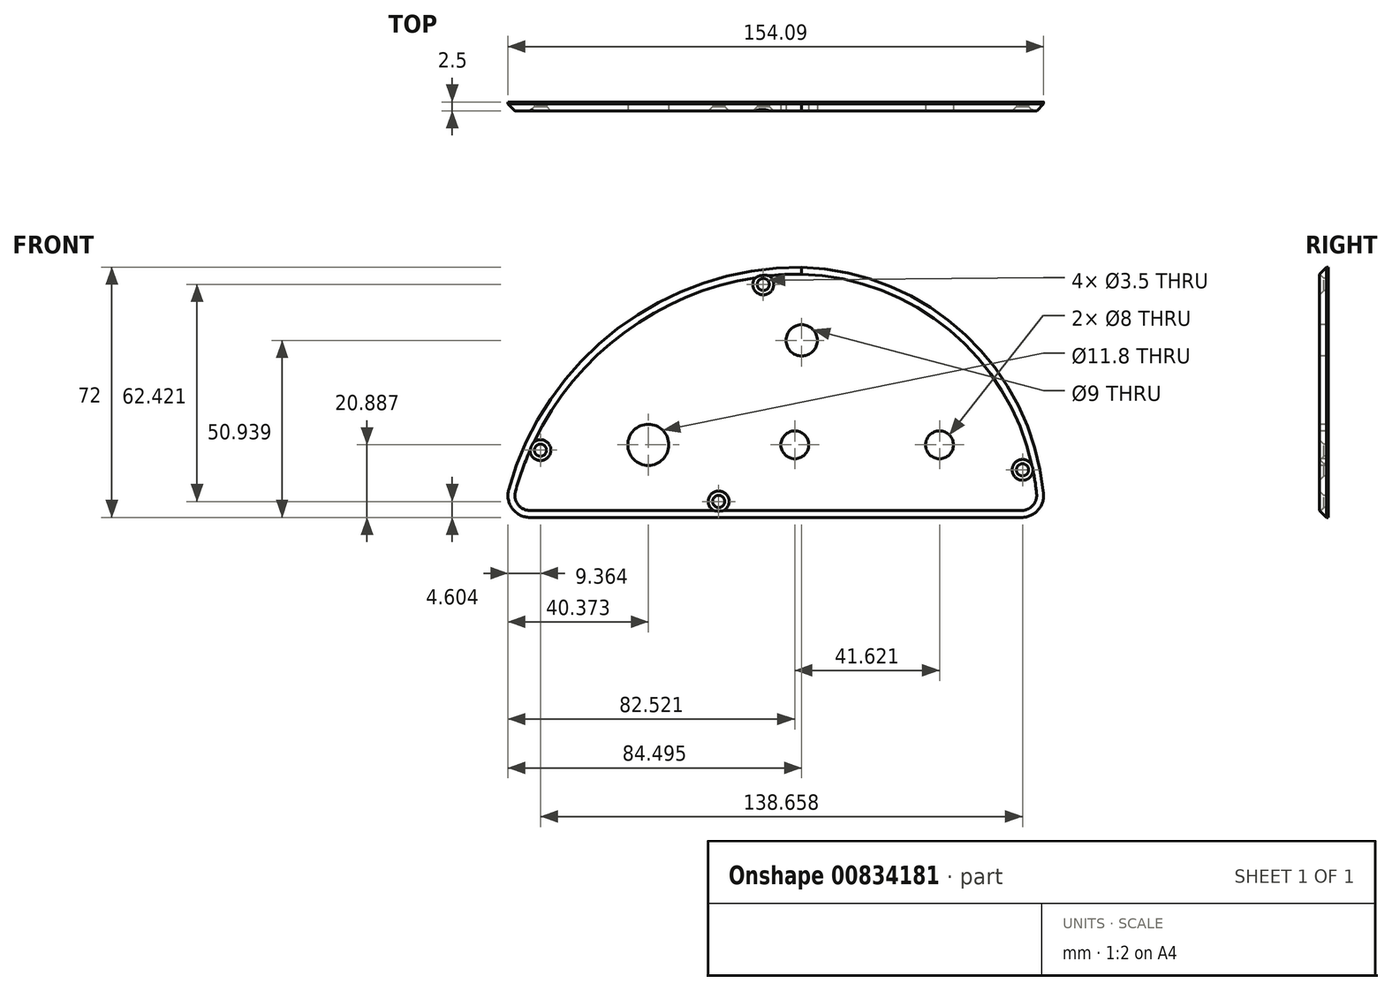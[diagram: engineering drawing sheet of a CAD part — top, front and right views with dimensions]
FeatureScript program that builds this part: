
annotation { "Feature Type Name" : "Feature", "Feature Type Description" : "" }
export const myFeature = defineFeature(function(context is Context, id is Id, definition is map)
    precondition{}
    {
        {
            var Q0;
            Q0=qCreatedBy(makeId("Front.planeOp"),FACE);
            var sketch = newSketch(context, id + "F0", { "sketchPlane" : qUnion([Q0])});
            skLineSegment(sketch, "E0", {"start": v(-103.73, 0) * mm, "end": v(52.27, 0) * mm, "construction": true});
            skLineSegment(sketch, "E1", {"start": v(-103.64, 41.04) * mm, "end": v(-17.64, 41.04) * mm, "construction": true});
            skLineSegment(sketch, "E2", {"start": v(-17.64, 0) * mm, "end": v(-17.64, 72) * mm, "construction": true});
            skArc(sketch, "E3", {"start": v(-17.64, 72) * mm, "mid": v(-70.6, 54.28) * mm, "end": v(-101.91, 8.04) * mm});
            skArc(sketch, "E4", {"start": v(51.92, 6.98) * mm, "mid": v(29.37, 52.58) * mm, "end": v(-17.64, 72) * mm});
            skLineSegment(sketch, "E5", {"start": v(-95.8, 0) * mm, "end": v(45.6, 0) * mm});
            skPoint(sketch, "E6.visualSharp", {"position": v(-103.73, 0) * mm});
            skArc(sketch, "E6.filletArc", {"start": v(-101.91, 8.04) * mm, "mid": v(-100.84, 2.5) * mm, "end": v(-95.8, 0) * mm});
            skPoint(sketch, "E7.visualSharp", {"position": v(52.27, 0) * mm});
            skArc(sketch, "E7.filletArc", {"start": v(45.6, 0) * mm, "mid": v(50.3, 2.09) * mm, "end": v(51.92, 6.98) * mm});
            skPoint(sketch, "E8", {"position": v(-28.7, 67.03) * mm});
            skPoint(sketch, "E9", {"position": v(-92.78, 19.37) * mm});
            skPoint(sketch, "E10", {"position": v(45.88, 13.7) * mm});
            skLineSegment(sketch, "E11", {"start": v(-73.3, 20.89) * mm, "end": v(34.06, 20.89) * mm, "construction": true});
            skPoint(sketch, "E12", {"position": v(-73.3, 20.89) * mm});
            skPoint(sketch, "E13", {"position": v(-19.62, 20.89) * mm});
            skPoint(sketch, "E14", {"position": v(22, 20.89) * mm});
            skPoint(sketch, "E15", {"position": v(-17.64, 50.94) * mm});
            skPoint(sketch, "E16", {"position": v(-61.77, 20.89) * mm});
            skPoint(sketch, "E17", {"position": v(-41.52, 0) * mm});
            skPoint(sketch, "E18", {"position": v(-41.52, 4.6) * mm});
            skSolve(sketch);
        }
        {
            var Q0;
            Q0=makeQuery(id+"F0.imprint","IMPRINT",FACE,{"disambiguationData":[TD([[makeQuery(id+"F0.imprint","IMPRINT",EDGE,{"derivedFrom":sQuery(id+"F0.wireOp",EDGE,"E3")}),1.0]])]});
            extrude(context, id + "F1", {"entities" : qUnion([Q0]), "oppositeDirection" : true, "depth" : 2.5 * mm, "offsetDistance" : 25 * mm});
        }
        {
            var Q0;
            Q0=sQuery(id+"F0.wireOp",VERTEX,"E9");
            var Q1;
            Q1=sQuery(id+"F0.wireOp",VERTEX,"E8");
            var Q2;
            Q2=sQuery(id+"F0.wireOp",VERTEX,"E10");
            var Q3;
            Q3=sQuery(id+"F0.wireOp",VERTEX,"E18");
            var Q4;
            Q4=makeQuery(id+"F1.opExtrude","SWEPT_BODY",BODY,{"disambiguationData":[OSD([sQuery(id+"F0.wireOp",EDGE,"E3"),sQuery(id+"F0.wireOp",EDGE,"E4"),sQuery(id+"F0.wireOp",EDGE,"E5"),sQuery(id+"F0.wireOp",EDGE,"E6.filletArc"),sQuery(id+"F0.wireOp",EDGE,"E7.filletArc")])]});
            hole(context, id + "F2", {"style" : HoleStyle.C_SINK, "endStyle" : HoleEndStyle.THROUGH, "holeDiameter" : 3.5 * mm, "cSinkDiameter" : 6 * mm, "cSinkAngle" : 90 * degree, "majorDiameter" : 5 * mm, "isTappedThrough" : true, "tappedDepth" : 12 * mm, "tapClearance" : 3, "locations" : qUnion([Q0, Q1, Q2, Q3]), "scope" : qUnion([Q4])});
        }
        {
            var Q0;
            Q0=makeQuery(id+"F1.opExtrude","CAP_EDGE",EDGE,{"disambiguationData":[OSD([sQuery(id+"F0.wireOp",EDGE,"E4")])],"isStart":true});
            chamfer(context, id + "F3", {"entities" : qUnion([Q0]), "width" : 2 * mm, "tangentPropagation" : true});
        }
        {
            var Q0;
            Q0=sQuery(id+"F0.wireOp",VERTEX,"E16");
            var Q1;
            Q1=makeQuery(id+"F1.opExtrude","SWEPT_BODY",BODY,{"disambiguationData":[OSD([sQuery(id+"F0.wireOp",EDGE,"E3"),sQuery(id+"F0.wireOp",EDGE,"E4"),sQuery(id+"F0.wireOp",EDGE,"E5"),sQuery(id+"F0.wireOp",EDGE,"E6.filletArc"),sQuery(id+"F0.wireOp",EDGE,"E7.filletArc")])]});
            hole(context, id + "F4", {"style" : HoleStyle.SIMPLE, "endStyle" : HoleEndStyle.THROUGH, "holeDiameter" : 11.8 * mm, "majorDiameter" : 5 * mm, "isTappedThrough" : true, "tappedDepth" : 12 * mm, "tapClearance" : 3, "locations" : qUnion([Q0]), "scope" : qUnion([Q1])});
        }
        {
            var Q0;
            Q0=sQuery(id+"F0.wireOp",VERTEX,"E13");
            var Q1;
            Q1=sQuery(id+"F0.wireOp",VERTEX,"E14");
            var Q2;
            Q2=makeQuery(id+"F1.opExtrude","SWEPT_BODY",BODY,{"disambiguationData":[OSD([sQuery(id+"F0.wireOp",EDGE,"E3"),sQuery(id+"F0.wireOp",EDGE,"E4"),sQuery(id+"F0.wireOp",EDGE,"E5"),sQuery(id+"F0.wireOp",EDGE,"E6.filletArc"),sQuery(id+"F0.wireOp",EDGE,"E7.filletArc")])]});
            hole(context, id + "F5", {"style" : HoleStyle.SIMPLE, "endStyle" : HoleEndStyle.THROUGH, "holeDiameter" : 8 * mm, "majorDiameter" : 5 * mm, "isTappedThrough" : true, "tappedDepth" : 12 * mm, "tapClearance" : 3, "locations" : qUnion([Q0, Q1]), "scope" : qUnion([Q2])});
        }
        {
            var Q0;
            Q0=sQuery(id+"F0.wireOp",VERTEX,"E15");
            var Q1;
            Q1=makeQuery(id+"F1.opExtrude","SWEPT_BODY",BODY,{"disambiguationData":[OSD([sQuery(id+"F0.wireOp",EDGE,"E3"),sQuery(id+"F0.wireOp",EDGE,"E4"),sQuery(id+"F0.wireOp",EDGE,"E5"),sQuery(id+"F0.wireOp",EDGE,"E6.filletArc"),sQuery(id+"F0.wireOp",EDGE,"E7.filletArc")])]});
            hole(context, id + "F6", {"style" : HoleStyle.SIMPLE, "endStyle" : HoleEndStyle.THROUGH, "holeDiameter" : 9 * mm, "majorDiameter" : 5 * mm, "isTappedThrough" : true, "tappedDepth" : 12 * mm, "tapClearance" : 3, "locations" : qUnion([Q0]), "scope" : qUnion([Q1])});
        }
    });
